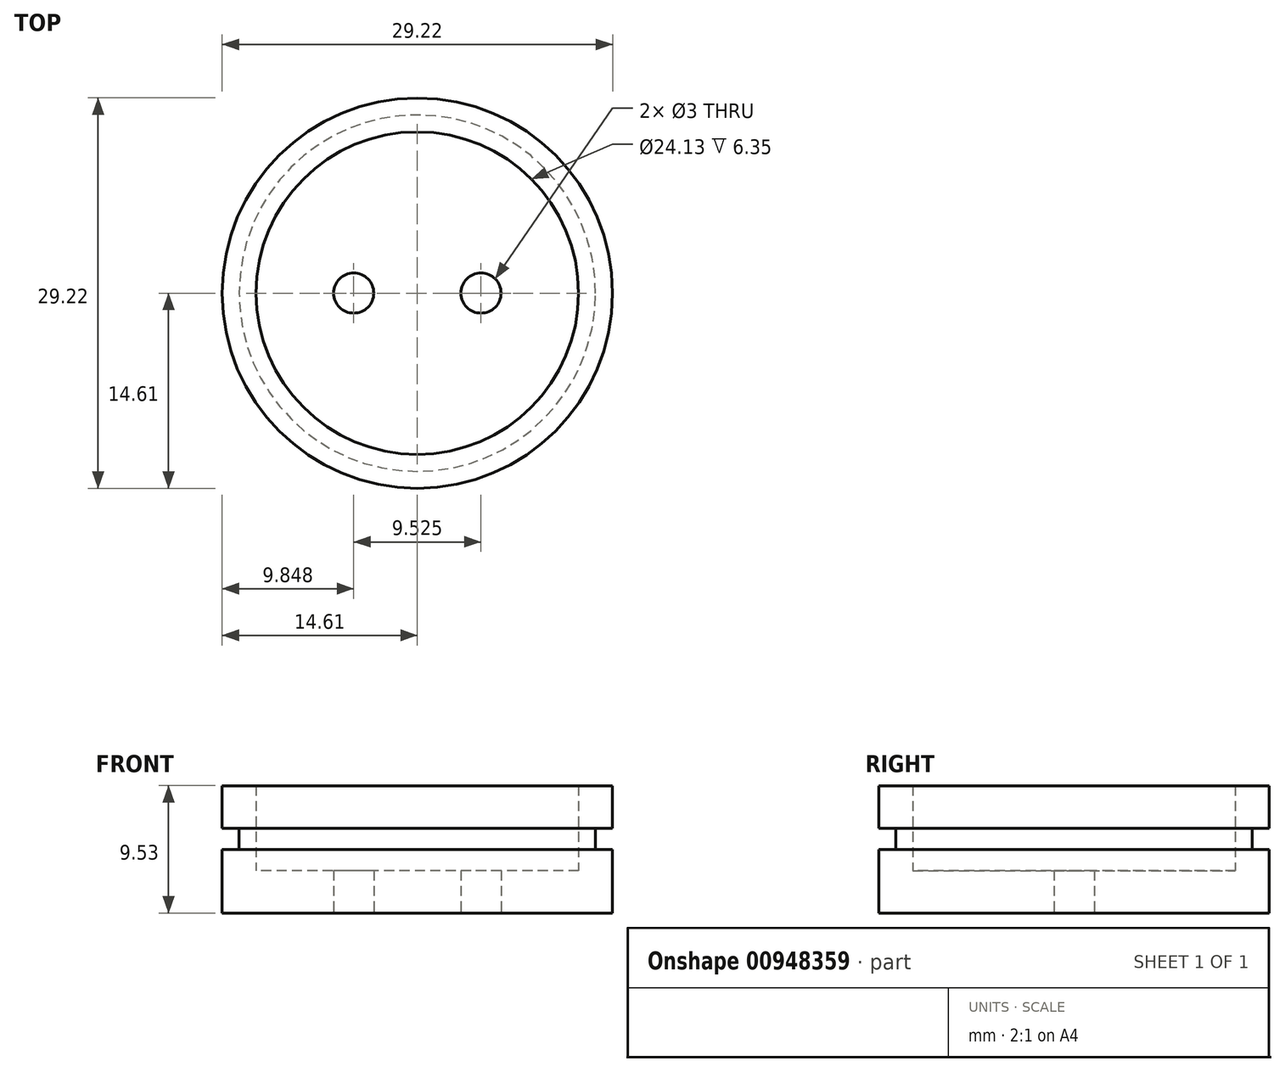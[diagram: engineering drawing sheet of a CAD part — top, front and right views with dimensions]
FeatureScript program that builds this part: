
annotation { "Feature Type Name" : "Feature", "Feature Type Description" : "" }
export const myFeature = defineFeature(function(context is Context, id is Id, definition is map)
    precondition{}
    {
        {
            var Q0;
            Q0=qCreatedBy(makeId("Top.planeOp"),FACE);
            var sketch = newSketch(context, id + "F0", { "sketchPlane" : qUnion([Q0])});
            skCircle(sketch, "E0", {"center": v(0, 0) * mm, "radius": 14.6 * mm});
            skCircle(sketch, "E1", {"center": v(-4.76, 0) * mm, "radius": 1.5 * mm});
            skCircle(sketch, "E2", {"center": v(4.76, 0) * mm, "radius": 1.5 * mm});
            skCircle(sketch, "E3", {"center": v(0, 0) * mm, "radius": 12.07 * mm});
            skSolve(sketch);
        }
        {
            var Q0;
            Q0 = qSketchRegion(id + "F0", true);
            extrude(context, id + "F1", {"entities" : qUnion([Q0]), "depth" : 9.52 * mm, "offsetDistance" : 25.4 * mm});
        }
        {
            var Q0;
            Q0=makeQuery(id+"F0.imprint","IMPRINT",FACE,{"disambiguationData":[TD([[makeQuery(id+"F0.imprint","IMPRINT",EDGE,{"derivedFrom":sQuery(id+"F0.wireOp",EDGE,"E1")}),-1.0]])]});
            extrude(context, id + "F2", {"entities" : qUnion([Q0]), "operationType" : NewBodyOperationType.ADD, "depth" : 3.17 * mm, "offsetDistance" : 25.4 * mm});
        }
        {
            var Q0;
            Q0=qCreatedBy(makeId("Top.planeOp"),FACE);
            cPlane(context, id + "F3", {"entities" : qUnion([Q0]), "cplaneType" : CPlaneType.OFFSET, "offset" : 6.35 * mm, "width" : 152.4 * mm, "height" : 152.4 * mm});
        }
        {
            var Q0;
            Q0=qCreatedBy(id+"F3.planeOp",FACE);
            var sketch = newSketch(context, id + "F4", { "sketchPlane" : qUnion([Q0])});
            skCircle(sketch, "E4", {"center": v(0, 0) * mm, "radius": 13.34 * mm});
            skCircle(sketch, "E5", {"center": v(0, 0) * mm, "radius": 18.38 * mm});
            skSolve(sketch);
        }
        {
            var Q0;
            Q0 = qSketchRegion(id + "F4", true);
            extrude(context, id + "F5", {"entities" : qUnion([Q0]), "operationType" : NewBodyOperationType.REMOVE, "oppositeDirection" : true, "depth" : 1.59 * mm, "offsetDistance" : 25.4 * mm});
        }
    });
